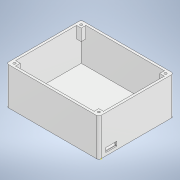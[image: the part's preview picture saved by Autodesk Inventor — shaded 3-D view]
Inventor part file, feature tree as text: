
AUTODESK INVENTOR PART (.ipt)
format: ipt  version: 2022 (Build 260153000, 153)  size: 207,360 bytes
history: native  units: mm
features: sketch x6, extrude x6, chamfer x2, other x1, fillet x1
ambient origin geometry x8: Origin, YZ Plane, XZ Plane, XY Plane, X Axis, Y Axis, Z Axis, Center Point
bodies: Body1 (feature_tree)
feature tree (16):
  other  "Těleso1"
  sketch  "Náčrt1"
  extrude  "Vysunutí1"  Depth=60.0mm
  extrude  "Vysunutí2"  Depth=75.0mm
  extrude  "Vysunutí3"  Depth=2.0mm
  extrude  "Vysunutí4"  Depth=2.0mm
  extrude  "Vysunutí5"  Depth=2.0mm
  extrude  "Vysunutí6"  Depth=2.0mm
  chamfer  "Zkosení1"  Distance=2.0mm
  chamfer  "Zkosení2"  Distance=32.0mm
  sketch  "Náčrt6"
  fillet  "Zaoblení1"  Radius=6.0mm
  sketch  "Náčrt2"
  sketch  "Náčrt3"
  sketch  "Náčrt4"
  sketch  "Náčrt5"
